# Revit family: Gira_108000
name_source: partatom
category: Elektroinstallationen
revit_build: Autodesk Revit 2017 (Build: 20160225_1515(x64)
units: mm (PartAtom-declared; Revit-internal decimal feet)

## family parameters
Basisbauteil = Fläche
Beim Laden mit Abzugskörper schneiden = Nein
Bemaßung runder Anschluss = Durchmesser verwenden
Beschriftungsausrichtung beibehalten = Nein
Gemeinsam genutzt = Nein
Raumberechnungspunkt = Nein
Teiletyp = Normal

## types (1)
- Gira_108000
    Andere Bussysteme = ohne
    Ausführung = USB
    Ausführung der Oberfläche = nicht zutreffend
    BIM = https://media.stage.bim.site X1 REG KNX.rfa
    Beschreibung = KNX USB Datenschnittstelle  REG Merkmale: - USB Datenschnittstelle mit integrierter Busankopplung. - Zur Ankopplung eines PCs an den KNX Bus um KNX Komponenten zu adressieren, programmieren oder diagnostizieren.  Hinweise : - Die Datenschnittstelle wird ab ETS3 unterstützt.
    Breite in Teilungseinheiten = 2
    Bussystem Funkbus = Nein
    Bussystem KNX = Ja
    Bussystem KNX-Funk = Nein
    Bussystem LON = Nein
    Bussystem Powernet = Nein
    DCF77 Empfänger integriert = Nein
    Datenblatt = https://katalog.gira.de
    Farbe = sonstige
    GTIN = 4010337080008
    HAN = 108000
    Hersteller = Gira
    IR-Sensor = Nein
    Logischer Baustein = Ja
    Mit Beschriftungsfeld = Nein
    Mit Busankopplung = Ja
    Mit Diebstahl-/Demontageschutz = Ja
    Mit Display = Ja
    Mit LED-Anzeige = Nein
    Montageart = REG
    Oberfläche = sonstige
    Produktseite = http://katalog.gira.de
    Präsenztaster = Nein
    Schutzart (IP) = IP20
    Status-LED = Ja
    Temperaturregler = Ja
    Transparent = Nein
    Typname = USB Datenschnittst. REG KNX REG
    URL = https://www.gira.de
    Vorgabe-Ansicht = 1219 mm
    Werkstoff = sonstige
    Werkstoffgüte = sonstige
    Zentrale Funktionseinheit für Sender/Aktoren = Ja

## geometry (parser evidence)
native form markers: Sweep x2
no freeform markers — native parametric forms only
